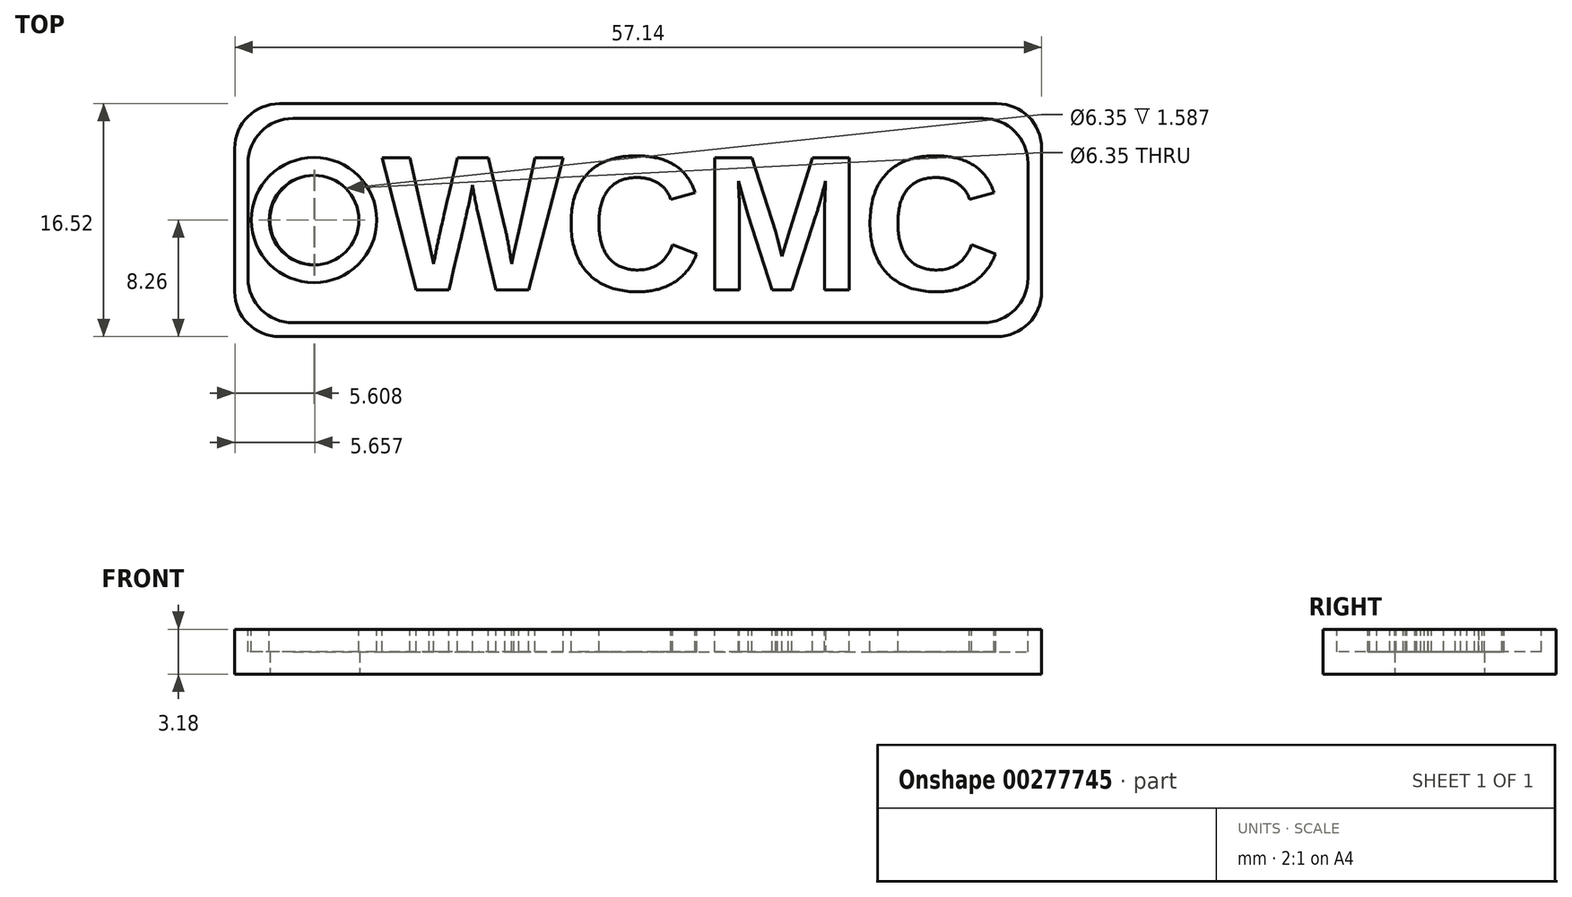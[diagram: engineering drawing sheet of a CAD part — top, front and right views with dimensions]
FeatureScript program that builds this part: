
annotation { "Feature Type Name" : "Feature", "Feature Type Description" : "" }
export const myFeature = defineFeature(function(context is Context, id is Id, definition is map)
    precondition{}
    {
        {
            var Q0;
            Q0=qCreatedBy(makeId("Top.planeOp"),FACE);
            var sketch = newSketch(context, id + "F0", { "sketchPlane" : qUnion([Q0])});
            skPoint(sketch, "E0.middle", {"position": v(0, 0) * mm});
            skCircle(sketch, "E1", {"center": v(-22.91, 0) * mm, "radius": 3.18 * mm});
            skLineSegment(sketch, "E2.bottom", {"start": v(25.4, -8.26) * mm, "end": v(-25.4, -8.26) * mm});
            skLineSegment(sketch, "E2.top", {"start": v(25.4, 8.26) * mm, "end": v(-25.4, 8.26) * mm});
            skLineSegment(sketch, "E2.left", {"start": v(28.58, -5.08) * mm, "end": v(28.58, 5.08) * mm});
            skLineSegment(sketch, "E2.right", {"start": v(-28.58, -5.08) * mm, "end": v(-28.58, 5.08) * mm});
            skPoint(sketch, "E3.visualSharp", {"position": v(-28.58, 8.26) * mm});
            skArc(sketch, "E3.filletArc", {"start": v(-25.4, 8.25) * mm, "mid": v(-27.65, 7.33) * mm, "end": v(-28.58, 5.08) * mm});
            skPoint(sketch, "E4.visualSharp", {"position": v(-28.58, -8.26) * mm});
            skArc(sketch, "E4.filletArc", {"start": v(-28.58, -5.08) * mm, "mid": v(-27.65, -7.33) * mm, "end": v(-25.4, -8.26) * mm});
            skPoint(sketch, "E5.visualSharp", {"position": v(28.58, -8.26) * mm});
            skArc(sketch, "E5.filletArc", {"start": v(25.4, -8.26) * mm, "mid": v(27.65, -7.33) * mm, "end": v(28.58, -5.08) * mm});
            skPoint(sketch, "E6.visualSharp", {"position": v(28.58, 8.26) * mm});
            skArc(sketch, "E6.filletArc", {"start": v(28.58, 5.08) * mm, "mid": v(27.65, 7.33) * mm, "end": v(25.4, 8.26) * mm});
            skSolve(sketch);
        }
        {
            var Q0;
            Q0 = qSketchRegion(id + "F0", true);
            extrude(context, id + "F1", {"entities" : qUnion([Q0]), "depth" : 3.17 * mm});
        }
        {
            var Q0;
            Q0=makeQuery(id+"F1.opExtrude","CAP_FACE",FACE,{"disambiguationData":[OSD([sQuery(id+"F0.wireOp",EDGE,"E0.bottom"),sQuery(id+"F0.wireOp",EDGE,"E0.top"),sQuery(id+"F0.wireOp",EDGE,"E0.left"),sQuery(id+"F0.wireOp",EDGE,"E0.right"),sQuery(id+"F0.wireOp",EDGE,"c47dbdb5-7af9-4379-a8ea-e0d7f1d22bdb.filletArc"),sQuery(id+"F0.wireOp",EDGE,"af2567a7-d5c6-4819-a93a-d2eca1756f1a.filletArc"),sQuery(id+"F0.wireOp",EDGE,"a5bfdc98-43ac-4b4a-890e-5966a53aafd6.filletArc"),sQuery(id+"F0.wireOp",EDGE,"1f3e9072-70dc-44ea-b174-963a890d8b17.filletArc"),sQuery(id+"F0.wireOp",EDGE,"E1")])],"isStart":false});
            var sketch = newSketch(context, id + "F2", { "sketchPlane" : qUnion([Q0])});
            skLineSegment(sketch, "E7.bottom", {"start": v(-24.46, 7.2) * mm, "end": v(24.43, 7.2) * mm});
            skLineSegment(sketch, "E7.top", {"start": v(-24.46, -7.28) * mm, "end": v(24.43, -7.28) * mm});
            skLineSegment(sketch, "E7.left", {"start": v(-27.64, 4.02) * mm, "end": v(-27.64, -4.1) * mm});
            skLineSegment(sketch, "E7.right", {"start": v(27.6, 4.02) * mm, "end": v(27.6, -4.1) * mm});
            skPoint(sketch, "E8.visualSharp", {"position": v(-27.64, 7.2) * mm});
            skArc(sketch, "E8.filletArc", {"start": v(-24.46, 7.2) * mm, "mid": v(-26.7, 6.27) * mm, "end": v(-27.64, 4.02) * mm});
            skPoint(sketch, "E9.visualSharp", {"position": v(-27.64, -7.28) * mm});
            skArc(sketch, "E9.filletArc", {"start": v(-27.64, -4.1) * mm, "mid": v(-26.7, -6.35) * mm, "end": v(-24.46, -7.28) * mm});
            skPoint(sketch, "E10.visualSharp", {"position": v(27.6, 7.2) * mm});
            skArc(sketch, "E10.filletArc", {"start": v(27.6, 4.02) * mm, "mid": v(26.68, 6.27) * mm, "end": v(24.43, 7.2) * mm});
            skPoint(sketch, "E11.visualSharp", {"position": v(27.6, -7.28) * mm});
            skArc(sketch, "E11.filletArc", {"start": v(24.43, -7.28) * mm, "mid": v(26.68, -6.35) * mm, "end": v(27.6, -4.1) * mm});
            skSolve(sketch);
        }
        {
            var Q0;
            Q0=makeQuery(id+"F2.imprint","IMPRINT",FACE,{"disambiguationData":[TD([[makeQuery(id+"F2.imprint","IMPRINT",EDGE,{"derivedFrom":sQuery(id+"F2.wireOp",EDGE,"E7.bottom")}),-1.0]])]});
            extrude(context, id + "F3", {"entities" : qUnion([Q0]), "operationType" : NewBodyOperationType.REMOVE, "oppositeDirection" : true, "depth" : 1.59 * mm});
        }
        {
            var Q0;
            Q0=makeQuery(id+"F2.imprint","IMPRINT",FACE,{"disambiguationData":[TD([[makeQuery(id+"F2.imprint","IMPRINT",EDGE,{"derivedFrom":sQuery(id+"F2.wireOp",EDGE,"E7.bottom")}),-1.0]])]});
            var sketch = newSketch(context, id + "F4", { "sketchPlane" : qUnion([Q0])});
            skText(sketch, "E12", { "text": "WCMC", "fontName": "Arimo-Bold.ttf"});
            skCircle(sketch, "E13", {"center": v(-22.96, 0) * mm, "radius": 4.44 * mm});
            skCircle(sketch, "E14", {"center": v(-22.96, 0) * mm, "radius": 3.18 * mm});
            const initialGuessF4  = {"E12": [-0.01816, -0.00495, 1, 0, 0.0098]};
            skSetInitialGuess(sketch, initialGuessF4);
            skSolve(sketch);
        }
        {
            var Q0;
            Q0 = qSketchRegion(id + "F4", true);
            extrude(context, id + "F5", {"entities" : qUnion([Q0]), "oppositeDirection" : true, "depth" : 1.59 * mm});
        }
    });
